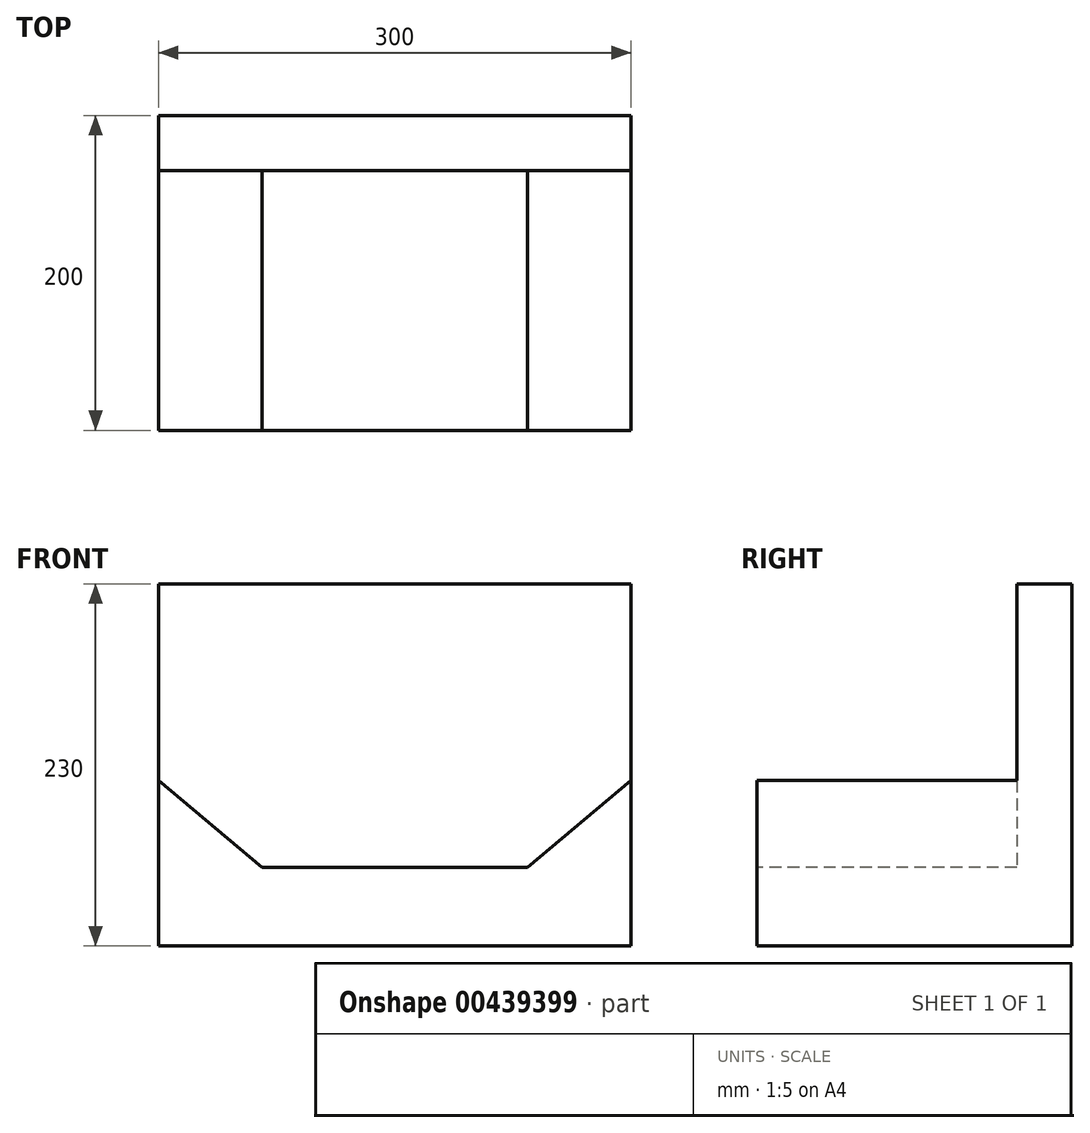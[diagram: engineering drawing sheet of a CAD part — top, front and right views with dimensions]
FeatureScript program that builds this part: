
annotation { "Feature Type Name" : "Feature", "Feature Type Description" : "" }
export const myFeature = defineFeature(function(context is Context, id is Id, definition is map)
    precondition{}
    {
        {
            var Q0;
            Q0=qCreatedBy(makeId("Front.planeOp"),FACE);
            var sketch = newSketch(context, id + "F0", { "sketchPlane" : qUnion([Q0])});
            skLineSegment(sketch, "E0.bottom", {"start": v(-113.38, -105.13) * mm, "end": v(186.62, -105.13) * mm});
            skLineSegment(sketch, "E0.top", {"start": v(-113.38, 124.87) * mm, "end": v(186.62, 124.87) * mm});
            skLineSegment(sketch, "E0.left", {"start": v(-113.38, -105.13) * mm, "end": v(-113.38, 124.87) * mm});
            skLineSegment(sketch, "E0.right", {"start": v(186.62, -105.13) * mm, "end": v(186.62, 124.87) * mm});
            skSolve(sketch);
        }
        {
            var Q0;
            Q0=makeQuery(id+"F0.imprint","IMPRINT",FACE,{"disambiguationData":[TD([[makeQuery(id+"F0.imprint","IMPRINT",EDGE,{"derivedFrom":sQuery(id+"F0.wireOp",EDGE,"E0.bottom")}),1.0]])]});
            extrude(context, id + "F1", {"entities" : qUnion([Q0]), "depth" : 200 * mm});
        }
        {
            var Q0;
            Q0=makeQuery(id+"F1.opExtrude","CAP_FACE",FACE,{"disambiguationData":[OSD([sQuery(id+"F0.wireOp",EDGE,"E0.bottom"),sQuery(id+"F0.wireOp",EDGE,"E0.top"),sQuery(id+"F0.wireOp",EDGE,"E0.left"),sQuery(id+"F0.wireOp",EDGE,"E0.right")])],"isStart":false});
            var sketch = newSketch(context, id + "F2", { "sketchPlane" : qUnion([Q0])});
            skLineSegment(sketch, "E1", {"start": v(-113.38, 0) * mm, "end": v(-47.67, -55.13) * mm});
            skLineSegment(sketch, "E2", {"start": v(-47.67, -55.13) * mm, "end": v(120.92, -55.13) * mm});
            skLineSegment(sketch, "E3", {"start": v(120.92, -55.13) * mm, "end": v(186.62, 0) * mm});
            skSolve(sketch);
        }
        {
            var Q0;
            {var subQ2=sQuery(id+"F2.wireOp",EDGE,"E1");Q0=makeQuery(id+"F2.imprint","IMPRINT",FACE,{"disambiguationData":[TD([[makeQuery(id+"F2.imprint","IMPRINT",EDGE,{"derivedFrom":subQ2}),1.0]])]});}
            extrude(context, id + "F3", {"entities" : qUnion([Q0]), "operationType" : NewBodyOperationType.REMOVE, "oppositeDirection" : true, "depth" : 165 * mm});
        }
    });
